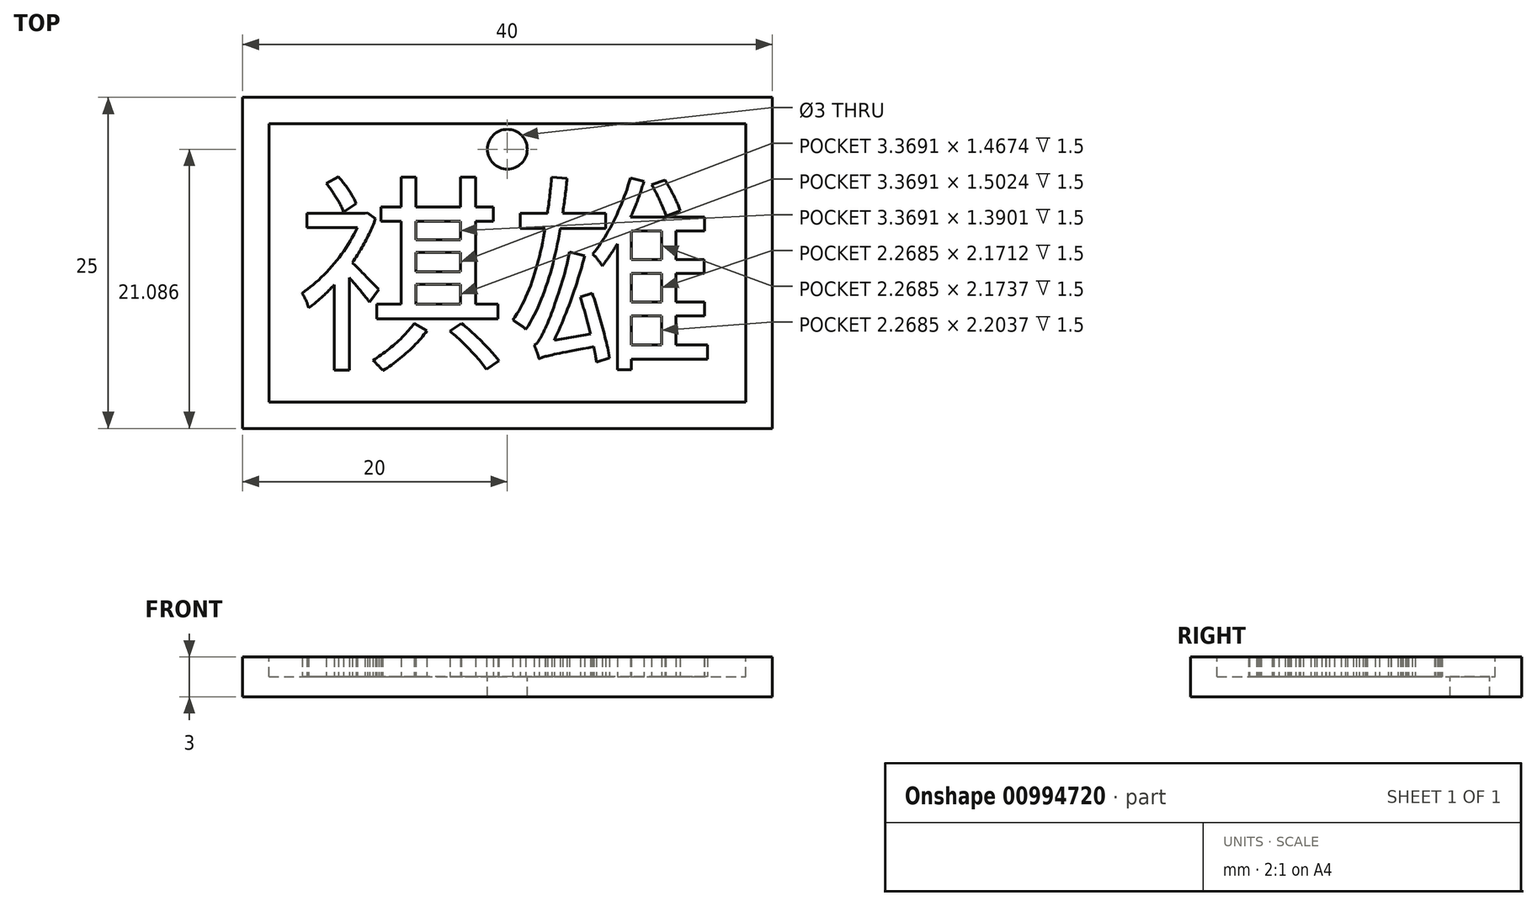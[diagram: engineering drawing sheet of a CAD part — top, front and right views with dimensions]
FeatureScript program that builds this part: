
annotation { "Feature Type Name" : "Feature", "Feature Type Description" : "" }
export const myFeature = defineFeature(function(context is Context, id is Id, definition is map)
    precondition{}
    {
        {
            var Q0;
            Q0=qCreatedBy(makeId("Top.planeOp"),FACE);
            var sketch = newSketch(context, id + "F0", { "sketchPlane" : qUnion([Q0])});
            skLineSegment(sketch, "E0.bottom", {"start": v(20, -12.5) * mm, "end": v(-20, -12.5) * mm});
            skLineSegment(sketch, "E0.top", {"start": v(20, 12.5) * mm, "end": v(-20, 12.5) * mm});
            skLineSegment(sketch, "E0.left", {"start": v(20, -12.5) * mm, "end": v(20, 12.5) * mm});
            skLineSegment(sketch, "E0.right", {"start": v(-20, -12.5) * mm, "end": v(-20, 12.5) * mm});
            skPoint(sketch, "E0.middle", {"position": v(0, 0) * mm});
            skSolve(sketch);
        }
        {
            var Q0;
            Q0 = qSketchRegion(id + "F0", true);
            extrude(context, id + "F1", {"entities" : qUnion([Q0]), "depth" : 3 * mm, "offsetDistance" : 25 * mm});
        }
        {
            var Q0;
            Q0=makeQuery(id+"F1.opExtrude","CAP_FACE",FACE,{"disambiguationData":[OSD([sQuery(id+"F0.wireOp",EDGE,"E0.bottom"),sQuery(id+"F0.wireOp",EDGE,"E0.top"),sQuery(id+"F0.wireOp",EDGE,"E0.left"),sQuery(id+"F0.wireOp",EDGE,"E0.right")])],"isStart":false});
            var sketch = newSketch(context, id + "F2", { "sketchPlane" : qUnion([Q0])});
            skLineSegment(sketch, "E1.0", {"start": v(18, -10.5) * mm, "end": v(18, 10.5) * mm});
            skLineSegment(sketch, "E1.1", {"start": v(-18, -10.5) * mm, "end": v(18, -10.5) * mm});
            skLineSegment(sketch, "E1.2", {"start": v(-18, 10.5) * mm, "end": v(-18, -10.5) * mm});
            skLineSegment(sketch, "E1.3", {"start": v(18, 10.5) * mm, "end": v(-18, 10.5) * mm});
            skSolve(sketch);
        }
        {
            var Q0;
            Q0 = qSketchRegion(id + "F2", true);
            extrude(context, id + "F3", {"entities" : qUnion([Q0]), "operationType" : NewBodyOperationType.REMOVE, "oppositeDirection" : true, "depth" : 1.5 * mm, "offsetDistance" : 25 * mm});
        }
        {
            var Q0;
            Q0=makeQuery(id+"F3.boolean.opBoolean","COPY",FACE,{"derivedFrom":makeQuery(id+"F3.opExtrude","CAP_FACE",FACE,{"disambiguationData":[OSD([sQuery(id+"F2.wireOp",EDGE,"E1.0"),sQuery(id+"F2.wireOp",EDGE,"E1.1"),sQuery(id+"F2.wireOp",EDGE,"E1.2"),sQuery(id+"F2.wireOp",EDGE,"E1.3")])],"isStart":false})});
            var sketch = newSketch(context, id + "F4", { "sketchPlane" : qUnion([Q0])});
            skCircle(sketch, "E2", {"center": v(0, 8.59) * mm, "radius": 1.5 * mm});
            skSolve(sketch);
        }
        {
            var Q0;
            Q0=makeQuery(id+"F4.imprint","IMPRINT",FACE,{"disambiguationData":[TD([[makeQuery(id+"F4.imprint","IMPRINT",EDGE,{"derivedFrom":sQuery(id+"F4.wireOp",EDGE,"E2")}),1.0]])]});
            extrude(context, id + "F5", {"entities" : qUnion([Q0]), "operationType" : NewBodyOperationType.REMOVE, "oppositeDirection" : true, "depth" : 1.5 * mm, "offsetDistance" : 25 * mm});
        }
        {
            var Q0;
            Q0=makeQuery(id+"F3.boolean.opBoolean","COPY",FACE,{"derivedFrom":makeQuery(id+"F3.opExtrude","CAP_FACE",FACE,{"disambiguationData":[OSD([sQuery(id+"F2.wireOp",EDGE,"E1.0"),sQuery(id+"F2.wireOp",EDGE,"E1.1"),sQuery(id+"F2.wireOp",EDGE,"E1.2"),sQuery(id+"F2.wireOp",EDGE,"E1.3")])],"isStart":false})});
            var sketch = newSketch(context, id + "F6", { "sketchPlane" : qUnion([Q0])});
            skText(sketch, "E3", { "text": "祺雄", "fontName": "NotoSansCJKtc-Regular.otf"});
            const initialGuessF6  = {"E3": [-0.016, -0.00688, 1, 0, 0.0115]};
            skSetInitialGuess(sketch, initialGuessF6);
            skSolve(sketch);
        }
        {
            var Q0;
            Q0 = qSketchRegion(id + "F6", true);
            extrude(context, id + "F7", {"entities" : qUnion([Q0]), "operationType" : NewBodyOperationType.ADD, "depth" : 1.5 * mm, "offsetDistance" : 25 * mm});
        }
    });
